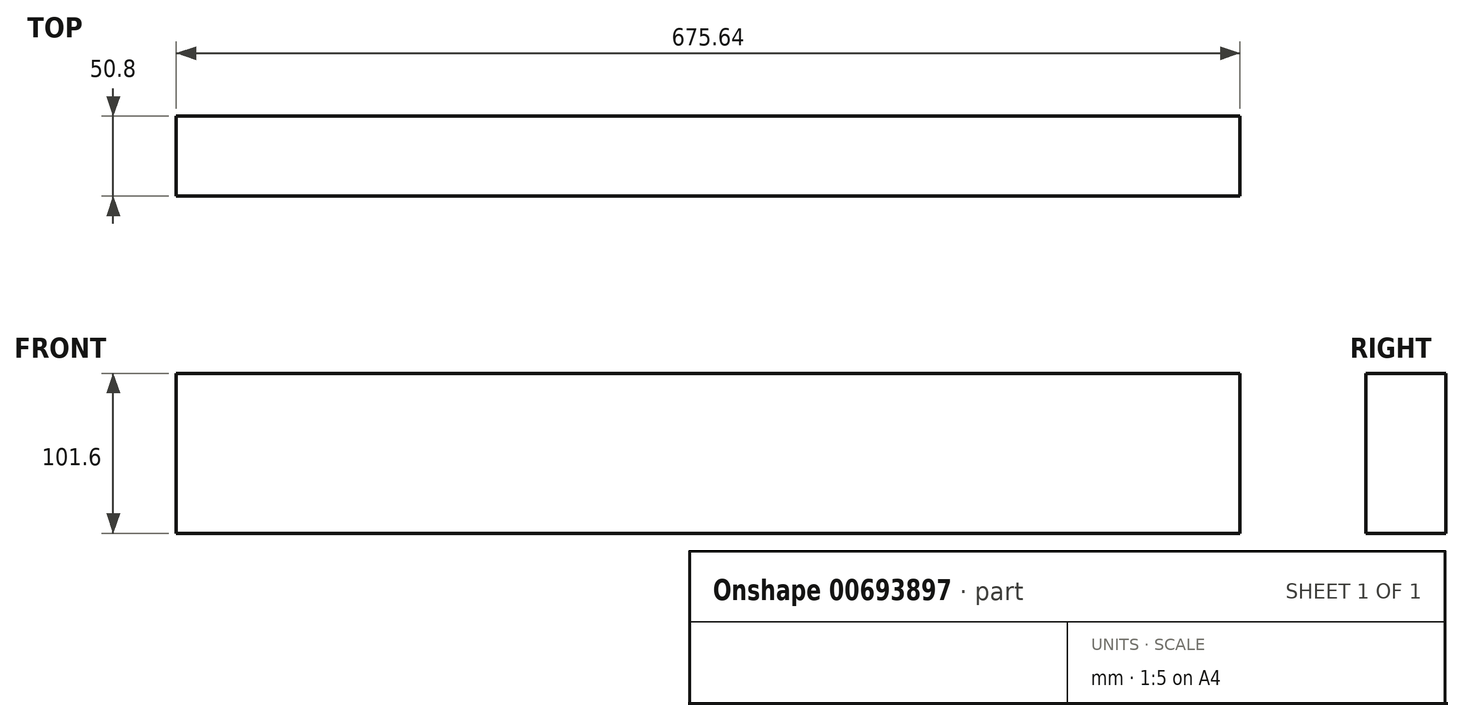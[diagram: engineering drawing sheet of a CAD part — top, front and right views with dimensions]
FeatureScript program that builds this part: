
annotation { "Feature Type Name" : "Feature", "Feature Type Description" : "" }
export const myFeature = defineFeature(function(context is Context, id is Id, definition is map)
    precondition{}
    {
        {
            var Q0;
            Q0=qCreatedBy(makeId("Right.planeOp"),FACE);
            var sketch = newSketch(context, id + "F0", { "sketchPlane" : qUnion([Q0])});
            skLineSegment(sketch, "E0.bottom", {"start": v(25.4, 50.8) * mm, "end": v(-25.4, 50.8) * mm});
            skLineSegment(sketch, "E0.top", {"start": v(25.4, -50.8) * mm, "end": v(-25.4, -50.8) * mm});
            skLineSegment(sketch, "E0.left", {"start": v(25.4, 50.8) * mm, "end": v(25.4, -50.8) * mm});
            skLineSegment(sketch, "E0.right", {"start": v(-25.4, 50.8) * mm, "end": v(-25.4, -50.8) * mm});
            skPoint(sketch, "E0.middle", {"position": v(0, 0) * mm});
            skSolve(sketch);
        }
        {
            var Q0;
            Q0=makeQuery(id+"F0.imprint","IMPRINT",FACE,{"disambiguationData":[TD([[makeQuery(id+"F0.imprint","IMPRINT",EDGE,{"derivedFrom":sQuery(id+"F0.wireOp",EDGE,"E0.bottom")}),1.0]])]});
            extrude(context, id + "F1", {"entities" : qUnion([Q0]), "depth" : 675.64 * mm, "offsetDistance" : 25.4 * mm});
        }
    });
